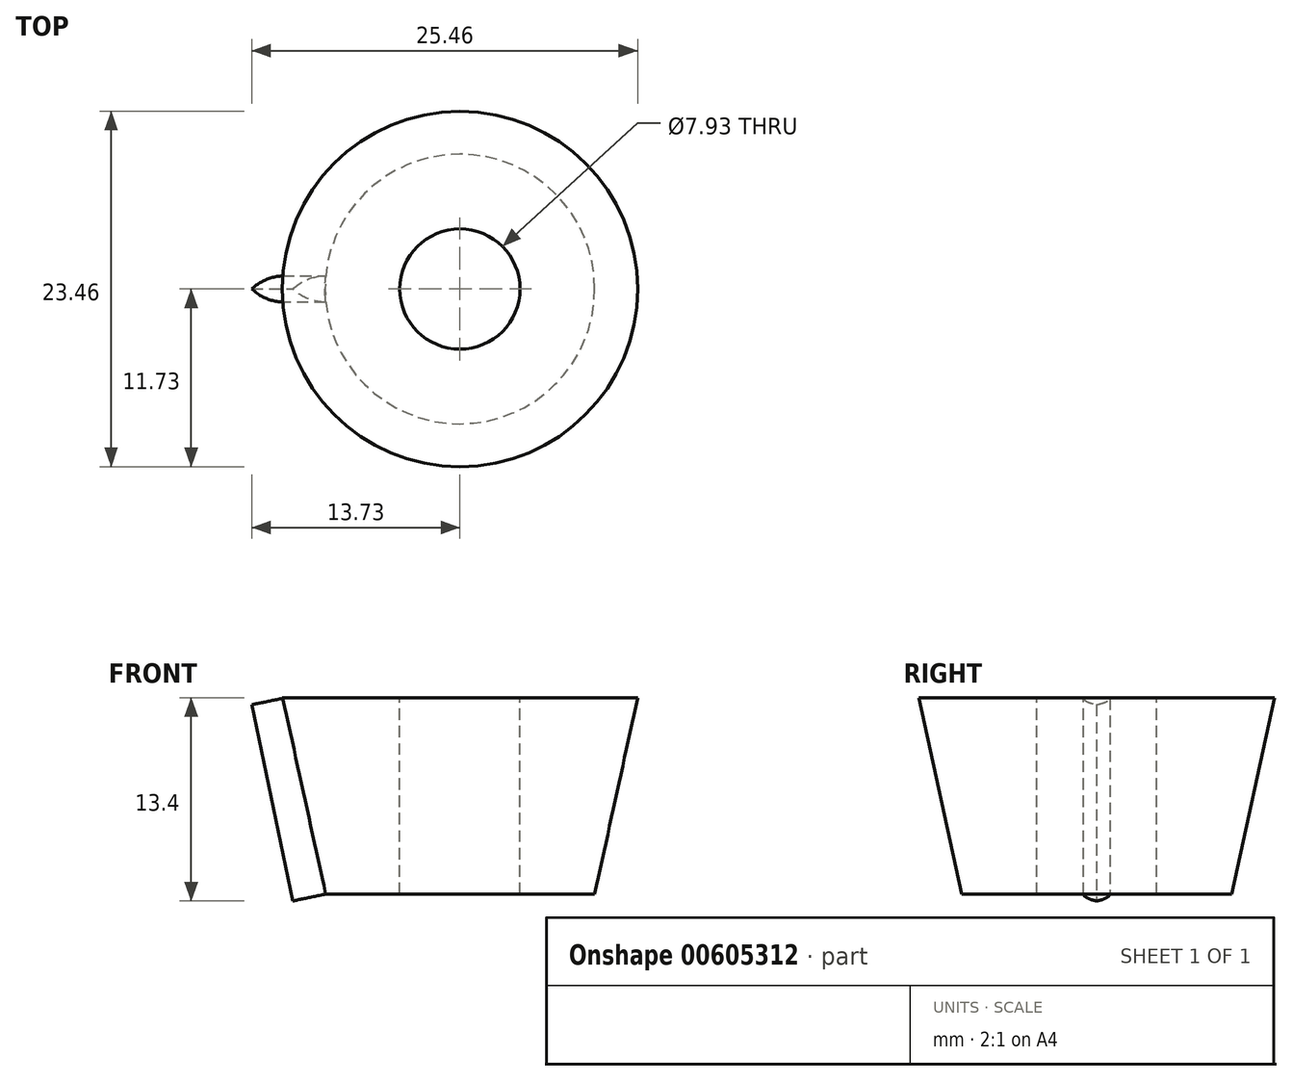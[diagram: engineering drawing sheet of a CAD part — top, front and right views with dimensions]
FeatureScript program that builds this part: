
annotation { "Feature Type Name" : "Feature", "Feature Type Description" : "" }
export const myFeature = defineFeature(function(context is Context, id is Id, definition is map)
    precondition{}
    {
        {
            var Q0;
            Q0=qCreatedBy(makeId("Top.planeOp"),FACE);
            var sketch = newSketch(context, id + "F0", { "sketchPlane" : qUnion([Q0])});
            skCircle(sketch, "E0", {"center": v(0, 0) * mm, "radius": 8.9 * mm});
            skSolve(sketch);
        }
        {
            var Q0;
            Q0=qCreatedBy(makeId("Top.planeOp"),FACE);
            cPlane(context, id + "F1", {"entities" : qUnion([Q0]), "cplaneType" : CPlaneType.OFFSET, "offset" : 12.95 * mm, "width" : 150 * mm, "height" : 150 * mm});
        }
        {
            var Q0;
            Q0=qCreatedBy(id+"F1.planeOp",FACE);
            var sketch = newSketch(context, id + "F2", { "sketchPlane" : qUnion([Q0])});
            skCircle(sketch, "E1", {"center": v(0, 0) * mm, "radius": 11.72 * mm});
            skSolve(sketch);
        }
        {
            var Q0;
            Q0=makeQuery(id+"F0.imprint","IMPRINT",FACE,{"disambiguationData":[TD([[makeQuery(id+"F0.imprint","IMPRINT",EDGE,{"derivedFrom":sQuery(id+"F0.wireOp",EDGE,"E0")}),1.0]])]});
            var Q1;
            Q1=makeQuery(id+"F2.imprint","IMPRINT",FACE,{"disambiguationData":[TD([[makeQuery(id+"F2.imprint","IMPRINT",EDGE,{"derivedFrom":sQuery(id+"F2.wireOp",EDGE,"E1")}),1.0]])]});
            loft(context, id + "F3", {"sheetProfilesArray" : [{ "sheetProfileEntities" : qUnion([Q0]) }, { "sheetProfileEntities" : qUnion([Q1]) }]});
        }
        {
            var Q0;
            Q0=makeQuery(id+"F3.opLoft","CAP_FACE",FACE,{"disambiguationData":[OSD([makeQuery(id+"F2.imprint","IMPRINT",FACE,{"disambiguationData":[TD([[makeQuery(id+"F2.imprint","IMPRINT",EDGE,{"derivedFrom":sQuery(id+"F2.wireOp",EDGE,"E1")}),1.0]])]})])],"isStart":true});
            var sketch = newSketch(context, id + "F4", { "sketchPlane" : qUnion([Q0])});
            skCircle(sketch, "E2", {"center": v(0, 0) * mm, "radius": 3.96 * mm});
            skSolve(sketch);
        }
        {
            var Q0;
            Q0=makeQuery(id+"F4.imprint","IMPRINT",FACE,{"disambiguationData":[TD([[makeQuery(id+"F4.imprint","IMPRINT",EDGE,{"derivedFrom":sQuery(id+"F4.wireOp",EDGE,"E2")}),1.0]])]});
            extrude(context, id + "F5", {"entities" : qUnion([Q0]), "operationType" : NewBodyOperationType.REMOVE, "oppositeDirection" : true, "depth" : 12.95 * mm, "offsetDistance" : 25 * mm});
        }
        {
            var Q0;
            Q0=makeQuery(id+"F3.opLoft","CAP_FACE",FACE,{"disambiguationData":[OSD([makeQuery(id+"F0.imprint","IMPRINT",FACE,{"disambiguationData":[TD([[makeQuery(id+"F0.imprint","IMPRINT",EDGE,{"derivedFrom":sQuery(id+"F0.wireOp",EDGE,"E0")}),1.0]])]})])],"isStart":true});
            var sketch = newSketch(context, id + "F6", { "sketchPlane" : qUnion([Q0])});
            skLineSegment(sketch, "E3", {"start": v(-8.87, 11.23) * mm, "end": v(-8.87, -11.27) * mm});
            skSolve(sketch);
        }
        {
            var Q0;
            Q0=qCreatedBy(makeId("Top.planeOp"),FACE);
            var Q1;
            Q1=sQuery(id+"F6.wireOp",EDGE,"E3");
            cPlane(context, id + "F7", {"entities" : qUnion([Q0, Q1]), "cplaneType" : CPlaneType.LINE_ANGLE, "offset" : 25 * mm, "angle" : 11.8 * degree, "oppositeDirection" : true, "width" : 150 * mm, "height" : 150 * mm});
        }
        {
            var Q0;
            Q0=qCreatedBy(id+"F7.planeOp",FACE);
            var sketch = newSketch(context, id + "F8", { "sketchPlane" : qUnion([Q0])});
            skArc(sketch, "E4", {"start": v(-10.89, 0) * mm, "mid": v(-9.86, -0.64) * mm, "end": v(-8.67, -0.87) * mm});
            skArc(sketch, "E5", {"start": v(-8.67, 0.87) * mm, "mid": v(-9.86, 0.64) * mm, "end": v(-10.89, 0) * mm});
            skArc(sketch, "E6", {"start": v(-8.67, -0.87) * mm, "mid": v(-8.7, 0) * mm, "end": v(-8.67, 0.87) * mm});
            skSolve(sketch);
        }
        {
            var Q0;
            Q0=makeQuery(id+"F8.imprint","IMPRINT",FACE,{"disambiguationData":[TD([[makeQuery(id+"F8.imprint","IMPRINT",EDGE,{"derivedFrom":sQuery(id+"F8.wireOp",EDGE,"E4")}),1.0]])]});
            extrude(context, id + "F9", {"entities" : qUnion([Q0]), "operationType" : NewBodyOperationType.ADD, "oppositeDirection" : true, "depth" : 13.22 * mm, "offsetDistance" : 25 * mm});
        }
    });
